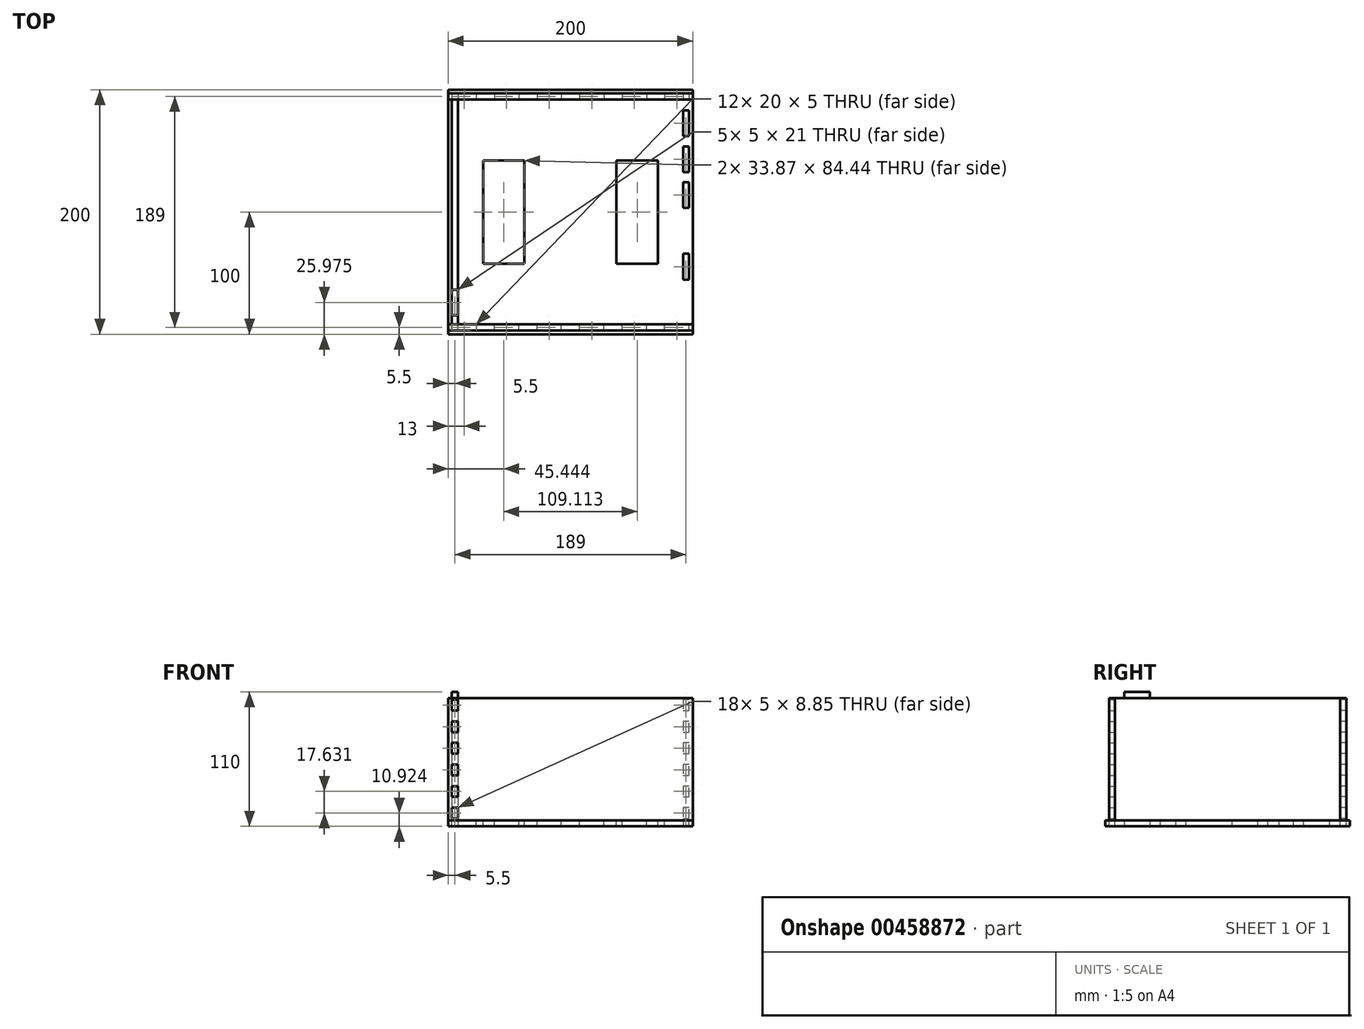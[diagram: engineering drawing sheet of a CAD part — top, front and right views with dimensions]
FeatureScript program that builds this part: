
annotation { "Feature Type Name" : "Feature", "Feature Type Description" : "" }
export const myFeature = defineFeature(function(context is Context, id is Id, definition is map)
    precondition{}
    {
        {
            assignVariable(context, id + "F0", {"name" : "width", "anyValue" : 5});
        }
        {
            var Q0;
            Q0=qCreatedBy(makeId("Top.planeOp"),FACE);
            var sketch = newSketch(context, id + "F1", { "sketchPlane" : qUnion([Q0])});
            skLineSegment(sketch, "E0.bottom", {"start": v(100, -100) * mm, "end": v(-100, -100) * mm});
            skLineSegment(sketch, "E0.top", {"start": v(100, 100) * mm, "end": v(-100, 100) * mm});
            skLineSegment(sketch, "E0.left", {"start": v(100, -100) * mm, "end": v(100, 100) * mm});
            skLineSegment(sketch, "E0.right", {"start": v(-100, -100) * mm, "end": v(-100, 100) * mm});
            skPoint(sketch, "E0.middle", {"position": v(0, 0) * mm});
            skLineSegment(sketch, "E1.0", {"start": v(97, 97) * mm, "end": v(-97, 97) * mm, "construction": true});
            skLineSegment(sketch, "E1.1", {"start": v(97, -97) * mm, "end": v(97, 97) * mm, "construction": true});
            skLineSegment(sketch, "E1.2", {"start": v(97, -97) * mm, "end": v(-97, -97) * mm, "construction": true});
            skLineSegment(sketch, "E1.3", {"start": v(-97, -97) * mm, "end": v(-97, 97) * mm, "construction": true});
            skSolve(sketch);
        }
        {
            var Q0;
            Q0 = qSketchRegion(id + "F1", true);
            extrude(context, id + "F2", {"entities" : qUnion([Q0]), "depth" : (getVariable(context, 'width')) * mm});
        }
        {
            var Q0;
            Q0=makeQuery(id+"F2.opExtrude","CAP_FACE",FACE,{"disambiguationData":[OSD([sQuery(id+"F1.wireOp",EDGE,"E0.bottom"),sQuery(id+"F1.wireOp",EDGE,"E0.top"),sQuery(id+"F1.wireOp",EDGE,"E0.left"),sQuery(id+"F1.wireOp",EDGE,"E0.right")])],"isStart":false});
            var sketch = newSketch(context, id + "F3", { "sketchPlane" : qUnion([Q0])});
            skLineSegment(sketch, "E2.0", {"start": v(97, 97) * mm, "end": v(-97, 97) * mm, "construction": true});
            skLineSegment(sketch, "E2.1", {"start": v(97, -97) * mm, "end": v(97, 97) * mm, "construction": true});
            skLineSegment(sketch, "E2.2", {"start": v(97, -97) * mm, "end": v(-97, -97) * mm, "construction": true});
            skLineSegment(sketch, "E2.3", {"start": v(-97, -97) * mm, "end": v(-97, 97) * mm, "construction": true});
            skLineSegment(sketch, "E3.bottom", {"start": v(-97, 97) * mm, "end": v(-77, 97) * mm, "construction": true});
            skLineSegment(sketch, "E3.left", {"start": v(-97, 97) * mm, "end": v(-97, 92) * mm, "construction": true});
            skLineSegment(sketch, "E4.bottom", {"start": v(-97, 97) * mm, "end": v(-77, 97) * mm});
            skLineSegment(sketch, "E4.top", {"start": v(-97, 92) * mm, "end": v(-77, 92) * mm});
            skLineSegment(sketch, "E4.left", {"start": v(-97, 97) * mm, "end": v(-97, 92) * mm});
            skLineSegment(sketch, "E4.right", {"start": v(-77, 97) * mm, "end": v(-77, 92) * mm});
            skLineSegment(sketch, "E5.1.0.0", {"start": v(-42.2, 97) * mm, "end": v(-42.2, 92) * mm});
            skLineSegment(sketch, "E5.1.0.1", {"start": v(-62.2, 92) * mm, "end": v(-42.2, 92) * mm});
            skLineSegment(sketch, "E5.1.0.2", {"start": v(-62.2, 97) * mm, "end": v(-42.2, 97) * mm});
            skLineSegment(sketch, "E5.1.0.3", {"start": v(-62.2, 97) * mm, "end": v(-62.2, 92) * mm});
            skLineSegment(sketch, "E5.2.0.0", {"start": v(-7.4, 97) * mm, "end": v(-7.4, 92) * mm});
            skLineSegment(sketch, "E5.2.0.1", {"start": v(-27.4, 92) * mm, "end": v(-7.4, 92) * mm});
            skLineSegment(sketch, "E5.2.0.2", {"start": v(-27.4, 97) * mm, "end": v(-7.4, 97) * mm});
            skLineSegment(sketch, "E5.2.0.3", {"start": v(-27.4, 97) * mm, "end": v(-27.4, 92) * mm});
            skLineSegment(sketch, "E5.3.0.0", {"start": v(27.4, 97) * mm, "end": v(27.4, 92) * mm});
            skLineSegment(sketch, "E5.3.0.1", {"start": v(7.4, 92) * mm, "end": v(27.4, 92) * mm});
            skLineSegment(sketch, "E5.3.0.2", {"start": v(7.4, 97) * mm, "end": v(27.4, 97) * mm});
            skLineSegment(sketch, "E5.3.0.3", {"start": v(7.4, 97) * mm, "end": v(7.4, 92) * mm});
            skLineSegment(sketch, "E5.4.0.0", {"start": v(62.2, 97) * mm, "end": v(62.2, 92) * mm});
            skLineSegment(sketch, "E5.4.0.1", {"start": v(42.2, 92) * mm, "end": v(62.2, 92) * mm});
            skLineSegment(sketch, "E5.4.0.2", {"start": v(42.2, 97) * mm, "end": v(62.2, 97) * mm});
            skLineSegment(sketch, "E5.4.0.3", {"start": v(42.2, 97) * mm, "end": v(42.2, 92) * mm});
            skLineSegment(sketch, "E5.5.0.0", {"start": v(97, 97) * mm, "end": v(97, 92) * mm});
            skLineSegment(sketch, "E5.5.0.1", {"start": v(77, 92) * mm, "end": v(97, 92) * mm});
            skLineSegment(sketch, "E5.5.0.2", {"start": v(77, 97) * mm, "end": v(97, 97) * mm});
            skLineSegment(sketch, "E5.5.0.3", {"start": v(77, 97) * mm, "end": v(77, 92) * mm});
            skLineSegment(sketch, "E5.direction1", {"start": v(-77, 92) * mm, "end": v(-42.2, 92) * mm, "construction": true});
            skLineSegment(sketch, "E6.MirrorCS", {"start": v(-97, -97) * mm, "end": v(-97, -92) * mm});
            skLineSegment(sketch, "E7.MirrorCS", {"start": v(-77, -97) * mm, "end": v(-77, -92) * mm});
            skLineSegment(sketch, "E8.MirrorCS", {"start": v(-97, -97) * mm, "end": v(-97, -92) * mm, "construction": true});
            skLineSegment(sketch, "E9.MirrorCS", {"start": v(97, -97) * mm, "end": v(97, -92) * mm});
            skLineSegment(sketch, "E10.MirrorCS", {"start": v(77, -97) * mm, "end": v(77, -92) * mm});
            skLineSegment(sketch, "E11.MirrorCS", {"start": v(-42.2, -97) * mm, "end": v(-42.2, -92) * mm});
            skLineSegment(sketch, "E12.MirrorCS", {"start": v(62.2, -97) * mm, "end": v(62.2, -92) * mm});
            skLineSegment(sketch, "E13.MirrorCS", {"start": v(-62.2, -97) * mm, "end": v(-62.2, -92) * mm});
            skLineSegment(sketch, "E14.MirrorCS", {"start": v(-7.4, -97) * mm, "end": v(-7.4, -92) * mm});
            skLineSegment(sketch, "E15.MirrorCS", {"start": v(-27.4, -97) * mm, "end": v(-27.4, -92) * mm});
            skLineSegment(sketch, "E16.MirrorCS", {"start": v(7.4, -97) * mm, "end": v(7.4, -92) * mm});
            skLineSegment(sketch, "E17.MirrorCS", {"start": v(27.4, -97) * mm, "end": v(27.4, -92) * mm});
            skLineSegment(sketch, "E18.MirrorCS", {"start": v(42.2, -97) * mm, "end": v(42.2, -92) * mm});
            skLineSegment(sketch, "E19.MirrorCS", {"start": v(-62.2, -92) * mm, "end": v(-42.2, -92) * mm});
            skLineSegment(sketch, "E20.MirrorCS", {"start": v(-27.4, -97) * mm, "end": v(-7.4, -97) * mm});
            skLineSegment(sketch, "E21.MirrorCS", {"start": v(7.4, -97) * mm, "end": v(27.4, -97) * mm});
            skLineSegment(sketch, "E22.MirrorCS", {"start": v(42.2, -97) * mm, "end": v(62.2, -97) * mm});
            skLineSegment(sketch, "E23.MirrorCS", {"start": v(77, -97) * mm, "end": v(97, -97) * mm});
            skLineSegment(sketch, "E24.MirrorCS", {"start": v(-62.2, -97) * mm, "end": v(-42.2, -97) * mm});
            skLineSegment(sketch, "E25.MirrorCS", {"start": v(-97, -97) * mm, "end": v(-77, -97) * mm});
            skLineSegment(sketch, "E26.MirrorCS", {"start": v(42.2, -92) * mm, "end": v(62.2, -92) * mm});
            skLineSegment(sketch, "E27.MirrorCS", {"start": v(77, -92) * mm, "end": v(97, -92) * mm});
            skLineSegment(sketch, "E28.MirrorCS", {"start": v(-77, -92) * mm, "end": v(-42.2, -92) * mm, "construction": true});
            skLineSegment(sketch, "E29.MirrorCS", {"start": v(-27.4, -92) * mm, "end": v(-7.4, -92) * mm});
            skLineSegment(sketch, "E30.MirrorCS", {"start": v(-97, -97) * mm, "end": v(-77, -97) * mm, "construction": true});
            skLineSegment(sketch, "E31.MirrorCS", {"start": v(-97, -92) * mm, "end": v(-77, -92) * mm});
            skLineSegment(sketch, "E32.MirrorCS", {"start": v(7.4, -92) * mm, "end": v(27.4, -92) * mm});
            skSolve(sketch);
        }
        {
            var Q0;
            Q0 = qSketchRegion(id + "F3", true);
            extrude(context, id + "F4", {"entities" : qUnion([Q0]), "operationType" : NewBodyOperationType.REMOVE, "oppositeDirection" : true, "depth" : 25 * mm});
        }
        {
            var Q0;
            Q0=makeQuery(id+"F2.opExtrude","CAP_FACE",FACE,{"disambiguationData":[OSD([sQuery(id+"F1.wireOp",EDGE,"E0.bottom"),sQuery(id+"F1.wireOp",EDGE,"E0.top"),sQuery(id+"F1.wireOp",EDGE,"E0.left"),sQuery(id+"F1.wireOp",EDGE,"E0.right")])],"isStart":false});
            var sketch = newSketch(context, id + "F5", { "sketchPlane" : qUnion([Q0])});
            skLineSegment(sketch, "E33.0", {"start": v(-97, 97) * mm, "end": v(-77, 97) * mm});
            skSolve(sketch);
        }
        {
            var Q0;
            Q0=makeQuery(id+"F5.imprint","IMPRINT",FACE,{"disambiguationData":[TD([[makeQuery(id+"F5.imprint","IMPRINT",EDGE,{"derivedFrom":makeQuery(id+"F4.boolean.opBoolean","COPY",EDGE,{"derivedFrom":makeQuery(id+"F4.opExtrude","CAP_EDGE",EDGE,{"disambiguationData":[OSD([sQuery(id+"F3.wireOp",EDGE,"E5.1.0.0")])],"isStart":true})})}),-1.0]])]});
            var Q1;
            Q1=makeQuery(id+"F5.imprint","IMPRINT",FACE,{"disambiguationData":[TD([[makeQuery(id+"F5.imprint","IMPRINT",EDGE,{"derivedFrom":sQuery(id+"F5.wireOp",EDGE,"E33.0")}),-1.0]])]});
            var Q2;
            Q2=makeQuery(id+"F5.imprint","IMPRINT",FACE,{"disambiguationData":[TD([[makeQuery(id+"F5.imprint","IMPRINT",EDGE,{"derivedFrom":makeQuery(id+"F4.boolean.opBoolean","COPY",EDGE,{"derivedFrom":makeQuery(id+"F4.opExtrude","CAP_EDGE",EDGE,{"disambiguationData":[OSD([sQuery(id+"F3.wireOp",EDGE,"E5.2.0.0")])],"isStart":true})})}),-1.0]])]});
            var Q3;
            Q3=makeQuery(id+"F5.imprint","IMPRINT",FACE,{"disambiguationData":[TD([[makeQuery(id+"F5.imprint","IMPRINT",EDGE,{"derivedFrom":makeQuery(id+"F4.boolean.opBoolean","COPY",EDGE,{"derivedFrom":makeQuery(id+"F4.opExtrude","CAP_EDGE",EDGE,{"disambiguationData":[OSD([sQuery(id+"F3.wireOp",EDGE,"E5.3.0.0")])],"isStart":true})})}),-1.0]])]});
            var Q4;
            Q4=makeQuery(id+"F5.imprint","IMPRINT",FACE,{"disambiguationData":[TD([[makeQuery(id+"F5.imprint","IMPRINT",EDGE,{"derivedFrom":makeQuery(id+"F4.boolean.opBoolean","COPY",EDGE,{"derivedFrom":makeQuery(id+"F4.opExtrude","CAP_EDGE",EDGE,{"disambiguationData":[OSD([sQuery(id+"F3.wireOp",EDGE,"E5.4.0.0")])],"isStart":true})})}),-1.0]])]});
            var Q5;
            Q5=makeQuery(id+"F5.imprint","IMPRINT",FACE,{"disambiguationData":[TD([[makeQuery(id+"F5.imprint","IMPRINT",EDGE,{"derivedFrom":makeQuery(id+"F4.boolean.opBoolean","COPY",EDGE,{"derivedFrom":makeQuery(id+"F4.opExtrude","CAP_EDGE",EDGE,{"disambiguationData":[OSD([sQuery(id+"F3.wireOp",EDGE,"E5.5.0.0")])],"isStart":true})})}),-1.0]])]});
            var Q6;
            Q6=makeQuery(id+"F2.opExtrude","CAP_FACE",FACE,{"disambiguationData":[OSD([sQuery(id+"F1.wireOp",EDGE,"E0.bottom"),sQuery(id+"F1.wireOp",EDGE,"E0.top"),sQuery(id+"F1.wireOp",EDGE,"E0.left"),sQuery(id+"F1.wireOp",EDGE,"E0.right")])],"isStart":true});
            extrude(context, id + "F6", {"entities" : qUnion([Q0, Q1, Q2, Q3, Q4, Q5]), "endBound" : BoundingType.UP_TO_SURFACE, "oppositeDirection" : true, "endBoundEntityFace" : qUnion([Q6]), "depth" : 25 * mm});
        }
        {
            var Q0;
            Q0=makeQuery(id+"F2.opExtrude","CAP_FACE",FACE,{"disambiguationData":[OSD([sQuery(id+"F1.wireOp",EDGE,"E0.bottom"),sQuery(id+"F1.wireOp",EDGE,"E0.top"),sQuery(id+"F1.wireOp",EDGE,"E0.left"),sQuery(id+"F1.wireOp",EDGE,"E0.right")])],"isStart":false});
            var sketch = newSketch(context, id + "F7", { "sketchPlane" : qUnion([Q0])});
            skLineSegment(sketch, "E34.bottom", {"start": v(-100, 97) * mm, "end": v(100, 97) * mm});
            skLineSegment(sketch, "E34.top", {"start": v(-100, 92) * mm, "end": v(100, 92) * mm});
            skLineSegment(sketch, "E34.left", {"start": v(-100, 97) * mm, "end": v(-100, 92) * mm});
            skLineSegment(sketch, "E34.right", {"start": v(100, 97) * mm, "end": v(100, 92) * mm});
            skSolve(sketch);
        }
        {
            var Q0;
            Q0 = qSketchRegion(id + "F7", true);
            extrude(context, id + "F8", {"entities" : qUnion([Q0]), "depth" : 100 * mm});
        }
        {
            var Q0;
            Q0=makeQuery(id+"F2.opExtrude","CAP_FACE",FACE,{"disambiguationData":[OSD([sQuery(id+"F1.wireOp",EDGE,"E0.bottom"),sQuery(id+"F1.wireOp",EDGE,"E0.top"),sQuery(id+"F1.wireOp",EDGE,"E0.left"),sQuery(id+"F1.wireOp",EDGE,"E0.right")])],"isStart":true});
            var sketch = newSketch(context, id + "F9", { "sketchPlane" : qUnion([Q0])});
            skLineSegment(sketch, "E35.0", {"start": v(97, 97) * mm, "end": v(97, -97) * mm});
            skLineSegment(sketch, "E35.1", {"start": v(97, 97) * mm, "end": v(-97, 97) * mm});
            skLineSegment(sketch, "E35.2", {"start": v(-97, 97) * mm, "end": v(-97, -97) * mm});
            skLineSegment(sketch, "E35.3", {"start": v(97, -97) * mm, "end": v(-97, -97) * mm});
            skLineSegment(sketch, "E36.bottom", {"start": v(-97, 84.52) * mm, "end": v(-92, 84.52) * mm});
            skLineSegment(sketch, "E36.top", {"start": v(-97, 63.52) * mm, "end": v(-92, 63.52) * mm});
            skLineSegment(sketch, "E36.left", {"start": v(-97, 84.52) * mm, "end": v(-97, 63.52) * mm});
            skLineSegment(sketch, "E36.right", {"start": v(-92, 84.52) * mm, "end": v(-92, 63.52) * mm});
            skLineSegment(sketch, "E37.1.0.0", {"start": v(-97, 55.22) * mm, "end": v(-97, 34.22) * mm});
            skLineSegment(sketch, "E37.1.0.1", {"start": v(-97, 55.22) * mm, "end": v(-92, 55.22) * mm});
            skLineSegment(sketch, "E37.1.0.2", {"start": v(-97, 34.22) * mm, "end": v(-92, 34.22) * mm});
            skLineSegment(sketch, "E37.1.0.3", {"start": v(-92, 55.22) * mm, "end": v(-92, 34.22) * mm});
            skLineSegment(sketch, "E37.2.0.0", {"start": v(-97, 25.91) * mm, "end": v(-97, 4.91) * mm});
            skLineSegment(sketch, "E37.2.0.1", {"start": v(-97, 25.91) * mm, "end": v(-92, 25.91) * mm});
            skLineSegment(sketch, "E37.2.0.2", {"start": v(-97, 4.91) * mm, "end": v(-92, 4.91) * mm});
            skLineSegment(sketch, "E37.2.0.3", {"start": v(-92, 25.91) * mm, "end": v(-92, 4.91) * mm});
            skLineSegment(sketch, "E37.3.0.0", {"start": v(-97, -3.4) * mm, "end": v(-97, -24.4) * mm});
            skLineSegment(sketch, "E37.3.0.1", {"start": v(-97, -3.4) * mm, "end": v(-92, -3.4) * mm});
            skLineSegment(sketch, "E37.3.0.2", {"start": v(-97, -24.4) * mm, "end": v(-92, -24.4) * mm});
            skLineSegment(sketch, "E37.3.0.3", {"start": v(-92, -3.4) * mm, "end": v(-92, -24.4) * mm});
            skLineSegment(sketch, "E37.4.0.0", {"start": v(-97, -32.7) * mm, "end": v(-97, -53.7) * mm});
            skLineSegment(sketch, "E37.4.0.1", {"start": v(-97, -32.7) * mm, "end": v(-92, -32.7) * mm});
            skLineSegment(sketch, "E37.4.0.2", {"start": v(-97, -53.7) * mm, "end": v(-92, -53.7) * mm});
            skLineSegment(sketch, "E37.4.0.3", {"start": v(-92, -32.7) * mm, "end": v(-92, -53.7) * mm});
            skLineSegment(sketch, "E37.5.0.0", {"start": v(-97, -62) * mm, "end": v(-97, -83) * mm});
            skLineSegment(sketch, "E37.5.0.1", {"start": v(-97, -62) * mm, "end": v(-92, -62) * mm});
            skLineSegment(sketch, "E37.5.0.2", {"start": v(-97, -83) * mm, "end": v(-92, -83) * mm});
            skLineSegment(sketch, "E37.5.0.3", {"start": v(-92, -62) * mm, "end": v(-92, -83) * mm});
            skLineSegment(sketch, "E37.direction1", {"start": v(-97, 63.52) * mm, "end": v(-97, 34.22) * mm, "construction": true});
            skLineSegment(sketch, "E38.MirrorCS", {"start": v(97, 84.52) * mm, "end": v(97, 63.52) * mm});
            skLineSegment(sketch, "E39.MirrorCS", {"start": v(97, 84.52) * mm, "end": v(92, 84.52) * mm});
            skLineSegment(sketch, "E40.MirrorCS", {"start": v(92, 84.52) * mm, "end": v(92, 63.52) * mm});
            skLineSegment(sketch, "E41.MirrorCS", {"start": v(97, 63.52) * mm, "end": v(92, 63.52) * mm});
            skLineSegment(sketch, "E42.MirrorCS", {"start": v(97, 55.22) * mm, "end": v(92, 55.22) * mm});
            skLineSegment(sketch, "E43.MirrorCS", {"start": v(92, 55.22) * mm, "end": v(92, 34.22) * mm});
            skLineSegment(sketch, "E44.MirrorCS", {"start": v(97, 63.52) * mm, "end": v(97, 34.22) * mm, "construction": true});
            skLineSegment(sketch, "E45.MirrorCS", {"start": v(97, 55.22) * mm, "end": v(97, 34.22) * mm});
            skLineSegment(sketch, "E46.MirrorCS", {"start": v(97, 25.91) * mm, "end": v(97, 4.91) * mm});
            skLineSegment(sketch, "E47.MirrorCS", {"start": v(97, 34.22) * mm, "end": v(92, 34.22) * mm});
            skLineSegment(sketch, "E48.MirrorCS", {"start": v(97, 25.91) * mm, "end": v(92, 25.91) * mm});
            skLineSegment(sketch, "E49.MirrorCS", {"start": v(92, 25.91) * mm, "end": v(92, 4.91) * mm});
            skLineSegment(sketch, "E50.MirrorCS", {"start": v(97, 4.91) * mm, "end": v(92, 4.91) * mm});
            skLineSegment(sketch, "E51.MirrorCS", {"start": v(97, -32.7) * mm, "end": v(92, -32.7) * mm});
            skLineSegment(sketch, "E52.MirrorCS", {"start": v(92, -32.7) * mm, "end": v(92, -53.7) * mm});
            skLineSegment(sketch, "E53.MirrorCS", {"start": v(97, -32.7) * mm, "end": v(97, -53.7) * mm});
            skLineSegment(sketch, "E54.MirrorCS", {"start": v(97, -53.7) * mm, "end": v(92, -53.7) * mm});
            skLineSegment(sketch, "E55.MirrorCS", {"start": v(97, -62) * mm, "end": v(92, -62) * mm});
            skLineSegment(sketch, "E56.MirrorCS", {"start": v(92, -62) * mm, "end": v(92, -83) * mm});
            skLineSegment(sketch, "E57.MirrorCS", {"start": v(97, -62) * mm, "end": v(97, -83) * mm});
            skLineSegment(sketch, "E58.MirrorCS", {"start": v(97, -83) * mm, "end": v(92, -83) * mm});
            skLineSegment(sketch, "E59.MirrorCS", {"start": v(92, -3.4) * mm, "end": v(92, -24.4) * mm});
            skLineSegment(sketch, "E60.MirrorCS", {"start": v(97, -3.4) * mm, "end": v(92, -3.4) * mm});
            skLineSegment(sketch, "E61.MirrorCS", {"start": v(97, -24.4) * mm, "end": v(92, -24.4) * mm});
            skLineSegment(sketch, "E62.MirrorCS", {"start": v(97, -3.4) * mm, "end": v(97, -24.4) * mm});
            skSolve(sketch);
        }
        {
            var Q0;
            Q0=makeQuery(id+"F9.imprint","IMPRINT",FACE,{"disambiguationData":[TD([[makeQuery(id+"F9.imprint","IMPRINT",EDGE,{"derivedFrom":sQuery(id+"F9.wireOp",EDGE,"E38.MirrorCS")}),-1.0]])]});
            var Q1;
            Q1=makeQuery(id+"F9.imprint","IMPRINT",FACE,{"disambiguationData":[TD([[makeQuery(id+"F9.imprint","IMPRINT",EDGE,{"derivedFrom":sQuery(id+"F9.wireOp",EDGE,"E42.MirrorCS")}),1.0]])]});
            var Q2;
            Q2=makeQuery(id+"F9.imprint","IMPRINT",FACE,{"disambiguationData":[TD([[makeQuery(id+"F9.imprint","IMPRINT",EDGE,{"derivedFrom":sQuery(id+"F9.wireOp",EDGE,"E46.MirrorCS")}),-1.0]])]});
            var Q3;
            Q3=makeQuery(id+"F9.imprint","IMPRINT",FACE,{"disambiguationData":[TD([[makeQuery(id+"F9.imprint","IMPRINT",EDGE,{"derivedFrom":sQuery(id+"F9.wireOp",EDGE,"E59.MirrorCS")}),1.0]])]});
            var Q4;
            Q4=makeQuery(id+"F9.imprint","IMPRINT",FACE,{"disambiguationData":[TD([[makeQuery(id+"F9.imprint","IMPRINT",EDGE,{"derivedFrom":sQuery(id+"F9.wireOp",EDGE,"E51.MirrorCS")}),1.0]])]});
            var Q5;
            Q5=makeQuery(id+"F9.imprint","IMPRINT",FACE,{"disambiguationData":[TD([[makeQuery(id+"F9.imprint","IMPRINT",EDGE,{"derivedFrom":sQuery(id+"F9.wireOp",EDGE,"E55.MirrorCS")}),1.0]])]});
            var Q6;
            Q6=makeQuery(id+"F9.imprint","IMPRINT",FACE,{"disambiguationData":[TD([[makeQuery(id+"F9.imprint","IMPRINT",EDGE,{"derivedFrom":sQuery(id+"F9.wireOp",EDGE,"E36.bottom")}),-1.0]])]});
            var Q7;
            Q7=makeQuery(id+"F9.imprint","IMPRINT",FACE,{"disambiguationData":[TD([[makeQuery(id+"F9.imprint","IMPRINT",EDGE,{"derivedFrom":sQuery(id+"F9.wireOp",EDGE,"E37.1.0.0")}),1.0]])]});
            var Q8;
            Q8=makeQuery(id+"F9.imprint","IMPRINT",FACE,{"disambiguationData":[TD([[makeQuery(id+"F9.imprint","IMPRINT",EDGE,{"derivedFrom":sQuery(id+"F9.wireOp",EDGE,"E37.2.0.0")}),1.0]])]});
            var Q9;
            Q9=makeQuery(id+"F9.imprint","IMPRINT",FACE,{"disambiguationData":[TD([[makeQuery(id+"F9.imprint","IMPRINT",EDGE,{"derivedFrom":sQuery(id+"F9.wireOp",EDGE,"E37.3.0.0")}),1.0]])]});
            var Q10;
            Q10=makeQuery(id+"F9.imprint","IMPRINT",FACE,{"disambiguationData":[TD([[makeQuery(id+"F9.imprint","IMPRINT",EDGE,{"derivedFrom":sQuery(id+"F9.wireOp",EDGE,"E37.4.0.0")}),1.0]])]});
            var Q11;
            Q11=makeQuery(id+"F9.imprint","IMPRINT",FACE,{"disambiguationData":[TD([[makeQuery(id+"F9.imprint","IMPRINT",EDGE,{"derivedFrom":sQuery(id+"F9.wireOp",EDGE,"E37.5.0.0")}),1.0]])]});
            extrude(context, id + "F10", {"entities" : qUnion([Q0, Q1, Q2, Q3, Q4, Q5, Q6, Q7, Q8, Q9, Q10, Q11]), "operationType" : NewBodyOperationType.REMOVE, "oppositeDirection" : true, "depth" : 25 * mm});
        }
        {
            var Q0;
            Q0=makeQuery(id+"F8.opExtrude","SWEPT_BODY",BODY,{"disambiguationData":[OSD([sQuery(id+"F7.wireOp",EDGE,"E34.bottom"),sQuery(id+"F7.wireOp",EDGE,"E34.top"),sQuery(id+"F7.wireOp",EDGE,"E34.left"),sQuery(id+"F7.wireOp",EDGE,"E34.right")])]});
            var Q1;
            Q1=makeQuery(id+"F6.opExtrude","SWEPT_BODY",BODY,{"disambiguationData":[OSD([sQuery(id+"F3.wireOp",EDGE,"E5.5.0.0"),sQuery(id+"F3.wireOp",EDGE,"E5.5.0.1"),sQuery(id+"F3.wireOp",EDGE,"E5.5.0.2"),sQuery(id+"F3.wireOp",EDGE,"E5.5.0.3")])]});
            var Q2;
            Q2=makeQuery(id+"F6.opExtrude","SWEPT_BODY",BODY,{"disambiguationData":[OSD([sQuery(id+"F3.wireOp",EDGE,"E5.4.0.0"),sQuery(id+"F3.wireOp",EDGE,"E5.4.0.1"),sQuery(id+"F3.wireOp",EDGE,"E5.4.0.2"),sQuery(id+"F3.wireOp",EDGE,"E5.4.0.3")])]});
            var Q3;
            Q3=makeQuery(id+"F6.opExtrude","SWEPT_BODY",BODY,{"disambiguationData":[OSD([sQuery(id+"F3.wireOp",EDGE,"E5.3.0.0"),sQuery(id+"F3.wireOp",EDGE,"E5.3.0.1"),sQuery(id+"F3.wireOp",EDGE,"E5.3.0.2"),sQuery(id+"F3.wireOp",EDGE,"E5.3.0.3")])]});
            var Q4;
            Q4=makeQuery(id+"F6.opExtrude","SWEPT_BODY",BODY,{"disambiguationData":[OSD([sQuery(id+"F3.wireOp",EDGE,"E5.2.0.0"),sQuery(id+"F3.wireOp",EDGE,"E5.2.0.1"),sQuery(id+"F3.wireOp",EDGE,"E5.2.0.2"),sQuery(id+"F3.wireOp",EDGE,"E5.2.0.3")])]});
            var Q5;
            Q5=makeQuery(id+"F6.opExtrude","SWEPT_BODY",BODY,{"disambiguationData":[OSD([sQuery(id+"F3.wireOp",EDGE,"E5.1.0.0"),sQuery(id+"F3.wireOp",EDGE,"E5.1.0.1"),sQuery(id+"F3.wireOp",EDGE,"E5.1.0.2"),sQuery(id+"F3.wireOp",EDGE,"E5.1.0.3")])]});
            var Q6;
            Q6=makeQuery(id+"F6.opExtrude","SWEPT_BODY",BODY,{"disambiguationData":[OSD([sQuery(id+"F3.wireOp",EDGE,"E4.top"),sQuery(id+"F3.wireOp",EDGE,"E4.left"),sQuery(id+"F3.wireOp",EDGE,"E4.right"),sQuery(id+"F5.wireOp",EDGE,"E33.0")])]});
            booleanBodies(context, id + "F11", {"operationType" : BooleanOperationType.UNION, "tools" : qUnion([Q0, Q1, Q2, Q3, Q4, Q5, Q6])});
        }
        {
            var Q0;
            Q0=makeQuery(id+"F11.opBoolean","MERGE",FACE,{"derivedFrom":[makeQuery(id+"F6.opExtrude","SWEPT_FACE",FACE,{"disambiguationData":[OSD([sQuery(id+"F3.wireOp",EDGE,"E4.top")])]}),makeQuery(id+"F6.opExtrude","SWEPT_FACE",FACE,{"disambiguationData":[OSD([sQuery(id+"F3.wireOp",EDGE,"E5.1.0.1")])]}),makeQuery(id+"F6.opExtrude","SWEPT_FACE",FACE,{"disambiguationData":[OSD([sQuery(id+"F3.wireOp",EDGE,"E5.2.0.1")])]}),makeQuery(id+"F6.opExtrude","SWEPT_FACE",FACE,{"disambiguationData":[OSD([sQuery(id+"F3.wireOp",EDGE,"E5.3.0.1")])]}),makeQuery(id+"F6.opExtrude","SWEPT_FACE",FACE,{"disambiguationData":[OSD([sQuery(id+"F3.wireOp",EDGE,"E5.4.0.1")])]}),makeQuery(id+"F6.opExtrude","SWEPT_FACE",FACE,{"disambiguationData":[OSD([sQuery(id+"F3.wireOp",EDGE,"E5.5.0.1")])]}),makeQuery(id+"F8.opExtrude","SWEPT_FACE",FACE,{"disambiguationData":[OSD([sQuery(id+"F7.wireOp",EDGE,"E34.top")])]})]});
            var sketch = newSketch(context, id + "F12", { "sketchPlane" : qUnion([Q0])});
            skLineSegment(sketch, "E63.bottom", {"start": v(-100, 105) * mm, "end": v(100, 105) * mm});
            skLineSegment(sketch, "E63.top", {"start": v(-100, 5) * mm, "end": v(100, 5) * mm});
            skLineSegment(sketch, "E63.left", {"start": v(-100, 105) * mm, "end": v(-100, 5) * mm});
            skLineSegment(sketch, "E63.right", {"start": v(100, 105) * mm, "end": v(100, 5) * mm});
            skLineSegment(sketch, "E64.bottom", {"start": v(-147, 8) * mm, "end": v(-142, 8) * mm});
            skLineSegment(sketch, "E64.top", {"start": v(-147, 18) * mm, "end": v(-142, 18) * mm});
            skLineSegment(sketch, "E64.left", {"start": v(-147, 8) * mm, "end": v(-147, 18) * mm});
            skLineSegment(sketch, "E64.right", {"start": v(-142, 8) * mm, "end": v(-142, 18) * mm});
            skLineSegment(sketch, "E65.1.0.0", {"start": v(-142, 24.8) * mm, "end": v(-142, 34.8) * mm});
            skLineSegment(sketch, "E65.1.0.1", {"start": v(-147, 34.8) * mm, "end": v(-142, 34.8) * mm});
            skLineSegment(sketch, "E65.1.0.2", {"start": v(-147, 24.8) * mm, "end": v(-147, 34.8) * mm});
            skLineSegment(sketch, "E65.1.0.3", {"start": v(-147, 24.8) * mm, "end": v(-142, 24.8) * mm});
            skLineSegment(sketch, "E65.2.0.0", {"start": v(-142, 41.6) * mm, "end": v(-142, 51.6) * mm});
            skLineSegment(sketch, "E65.2.0.1", {"start": v(-147, 51.6) * mm, "end": v(-142, 51.6) * mm});
            skLineSegment(sketch, "E65.2.0.2", {"start": v(-147, 41.6) * mm, "end": v(-147, 51.6) * mm});
            skLineSegment(sketch, "E65.2.0.3", {"start": v(-147, 41.6) * mm, "end": v(-142, 41.6) * mm});
            skLineSegment(sketch, "E65.3.0.0", {"start": v(-142, 58.4) * mm, "end": v(-142, 68.4) * mm});
            skLineSegment(sketch, "E65.3.0.1", {"start": v(-147, 68.4) * mm, "end": v(-142, 68.4) * mm});
            skLineSegment(sketch, "E65.3.0.2", {"start": v(-147, 58.4) * mm, "end": v(-147, 68.4) * mm});
            skLineSegment(sketch, "E65.3.0.3", {"start": v(-147, 58.4) * mm, "end": v(-142, 58.4) * mm});
            skLineSegment(sketch, "E65.4.0.0", {"start": v(-142, 75.2) * mm, "end": v(-142, 85.2) * mm});
            skLineSegment(sketch, "E65.4.0.1", {"start": v(-147, 85.2) * mm, "end": v(-142, 85.2) * mm});
            skLineSegment(sketch, "E65.4.0.2", {"start": v(-147, 75.2) * mm, "end": v(-147, 85.2) * mm});
            skLineSegment(sketch, "E65.4.0.3", {"start": v(-147, 75.2) * mm, "end": v(-142, 75.2) * mm});
            skLineSegment(sketch, "E65.5.0.0", {"start": v(-142, 92) * mm, "end": v(-142, 102) * mm});
            skLineSegment(sketch, "E65.5.0.1", {"start": v(-147, 102) * mm, "end": v(-142, 102) * mm});
            skLineSegment(sketch, "E65.5.0.2", {"start": v(-147, 92) * mm, "end": v(-147, 102) * mm});
            skLineSegment(sketch, "E65.5.0.3", {"start": v(-147, 92) * mm, "end": v(-142, 92) * mm});
            skLineSegment(sketch, "E65.direction1", {"start": v(-142, 8) * mm, "end": v(-142, 24.8) * mm, "construction": true});
            skLineSegment(sketch, "E66.MirrorCS", {"start": v(142, 92) * mm, "end": v(142, 102) * mm});
            skLineSegment(sketch, "E67.MirrorCS", {"start": v(147, 102) * mm, "end": v(142, 102) * mm});
            skLineSegment(sketch, "E68.MirrorCS", {"start": v(147, 92) * mm, "end": v(147, 102) * mm});
            skLineSegment(sketch, "E69.MirrorCS", {"start": v(147, 92) * mm, "end": v(142, 92) * mm});
            skLineSegment(sketch, "E70.MirrorCS", {"start": v(147, 51.6) * mm, "end": v(142, 51.6) * mm});
            skLineSegment(sketch, "E71.MirrorCS", {"start": v(147, 58.4) * mm, "end": v(142, 58.4) * mm});
            skLineSegment(sketch, "E72.MirrorCS", {"start": v(147, 75.2) * mm, "end": v(142, 75.2) * mm});
            skLineSegment(sketch, "E73.MirrorCS", {"start": v(147, 41.6) * mm, "end": v(142, 41.6) * mm});
            skLineSegment(sketch, "E74.MirrorCS", {"start": v(147, 18) * mm, "end": v(142, 18) * mm});
            skLineSegment(sketch, "E75.MirrorCS", {"start": v(147, 68.4) * mm, "end": v(142, 68.4) * mm});
            skLineSegment(sketch, "E76.MirrorCS", {"start": v(147, 85.2) * mm, "end": v(142, 85.2) * mm});
            skLineSegment(sketch, "E77.MirrorCS", {"start": v(147, 24.8) * mm, "end": v(142, 24.8) * mm});
            skLineSegment(sketch, "E78.MirrorCS", {"start": v(142, 75.2) * mm, "end": v(142, 85.2) * mm});
            skLineSegment(sketch, "E79.MirrorCS", {"start": v(147, 41.6) * mm, "end": v(147, 51.6) * mm});
            skLineSegment(sketch, "E80.MirrorCS", {"start": v(100, 5) * mm, "end": v(-100, 5) * mm});
            skLineSegment(sketch, "E81.MirrorCS", {"start": v(147, 8) * mm, "end": v(142, 8) * mm});
            skLineSegment(sketch, "E82.MirrorCS", {"start": v(147, 8) * mm, "end": v(147, 18) * mm});
            skLineSegment(sketch, "E83.MirrorCS", {"start": v(142, 8) * mm, "end": v(142, 24.8) * mm, "construction": true});
            skLineSegment(sketch, "E84.MirrorCS", {"start": v(142, 24.8) * mm, "end": v(142, 34.8) * mm});
            skLineSegment(sketch, "E85.MirrorCS", {"start": v(147, 34.8) * mm, "end": v(142, 34.8) * mm});
            skLineSegment(sketch, "E86.MirrorCS", {"start": v(147, 24.8) * mm, "end": v(147, 34.8) * mm});
            skLineSegment(sketch, "E87.MirrorCS", {"start": v(142, 41.6) * mm, "end": v(142, 51.6) * mm});
            skLineSegment(sketch, "E88.MirrorCS", {"start": v(142, 58.4) * mm, "end": v(142, 68.4) * mm});
            skLineSegment(sketch, "E89.MirrorCS", {"start": v(147, 58.4) * mm, "end": v(147, 68.4) * mm});
            skLineSegment(sketch, "E90.MirrorCS", {"start": v(147, 75.2) * mm, "end": v(147, 85.2) * mm});
            skLineSegment(sketch, "E91", {"start": v(142, 18) * mm, "end": v(142, 8) * mm});
            skSolve(sketch);
        }
        {
            var Q0;
            Q0=makeQuery(id+"F12.imprint","IMPRINT",FACE,{"disambiguationData":[TD([[makeQuery(id+"F12.imprint","IMPRINT",EDGE,{"derivedFrom":sQuery(id+"F12.wireOp",EDGE,"E65.5.0.0")}),1.0]])]});
            var Q1;
            Q1=makeQuery(id+"F12.imprint","IMPRINT",FACE,{"disambiguationData":[TD([[makeQuery(id+"F12.imprint","IMPRINT",EDGE,{"derivedFrom":sQuery(id+"F12.wireOp",EDGE,"E65.4.0.0")}),1.0]])]});
            var Q2;
            Q2=makeQuery(id+"F12.imprint","IMPRINT",FACE,{"disambiguationData":[TD([[makeQuery(id+"F12.imprint","IMPRINT",EDGE,{"derivedFrom":sQuery(id+"F12.wireOp",EDGE,"E65.3.0.0")}),1.0]])]});
            var Q3;
            Q3=makeQuery(id+"F12.imprint","IMPRINT",FACE,{"disambiguationData":[TD([[makeQuery(id+"F12.imprint","IMPRINT",EDGE,{"derivedFrom":sQuery(id+"F12.wireOp",EDGE,"E65.2.0.0")}),1.0]])]});
            var Q4;
            Q4=makeQuery(id+"F12.imprint","IMPRINT",FACE,{"disambiguationData":[TD([[makeQuery(id+"F12.imprint","IMPRINT",EDGE,{"derivedFrom":sQuery(id+"F12.wireOp",EDGE,"E65.1.0.0")}),1.0]])]});
            var Q5;
            Q5=makeQuery(id+"F12.imprint","IMPRINT",FACE,{"disambiguationData":[TD([[makeQuery(id+"F12.imprint","IMPRINT",EDGE,{"derivedFrom":sQuery(id+"F12.wireOp",EDGE,"E64.bottom")}),1.0]])]});
            var Q6;
            Q6=makeQuery(id+"F12.imprint","IMPRINT",FACE,{"disambiguationData":[TD([[makeQuery(id+"F12.imprint","IMPRINT",EDGE,{"derivedFrom":sQuery(id+"F12.wireOp",EDGE,"E66.MirrorCS")}),-1.0]])]});
            var Q7;
            Q7=makeQuery(id+"F12.imprint","IMPRINT",FACE,{"disambiguationData":[TD([[makeQuery(id+"F12.imprint","IMPRINT",EDGE,{"derivedFrom":sQuery(id+"F12.wireOp",EDGE,"E72.MirrorCS")}),-1.0]])]});
            var Q8;
            Q8=makeQuery(id+"F12.imprint","IMPRINT",FACE,{"disambiguationData":[TD([[makeQuery(id+"F12.imprint","IMPRINT",EDGE,{"derivedFrom":sQuery(id+"F12.wireOp",EDGE,"E71.MirrorCS")}),-1.0]])]});
            var Q9;
            Q9=makeQuery(id+"F12.imprint","IMPRINT",FACE,{"disambiguationData":[TD([[makeQuery(id+"F12.imprint","IMPRINT",EDGE,{"derivedFrom":sQuery(id+"F12.wireOp",EDGE,"E70.MirrorCS")}),1.0]])]});
            var Q10;
            Q10=makeQuery(id+"F12.imprint","IMPRINT",FACE,{"disambiguationData":[TD([[makeQuery(id+"F12.imprint","IMPRINT",EDGE,{"derivedFrom":sQuery(id+"F12.wireOp",EDGE,"E77.MirrorCS")}),-1.0]])]});
            var Q11;
            Q11=makeQuery(id+"F12.imprint","IMPRINT",FACE,{"disambiguationData":[TD([[makeQuery(id+"F12.imprint","IMPRINT",EDGE,{"derivedFrom":sQuery(id+"F12.wireOp",EDGE,"E82.MirrorCS")}),1.0]])]});
            extrude(context, id + "F13", {"entities" : qUnion([Q0, Q1, Q2, Q3, Q4, Q5, Q6, Q7, Q8, Q9, Q10, Q11]), "operationType" : NewBodyOperationType.REMOVE, "oppositeDirection" : true, "depth" : 25 * mm});
        }
        {
            var Q0;
            Q0=makeQuery(id+"F2.opExtrude","CAP_FACE",FACE,{"disambiguationData":[OSD([sQuery(id+"F1.wireOp",EDGE,"E0.bottom"),sQuery(id+"F1.wireOp",EDGE,"E0.top"),sQuery(id+"F1.wireOp",EDGE,"E0.left"),sQuery(id+"F1.wireOp",EDGE,"E0.right")])],"isStart":false});
            var sketch = newSketch(context, id + "F14", { "sketchPlane" : qUnion([Q0])});
            skLineSegment(sketch, "E92.bottom", {"start": v(-97, 92) * mm, "end": v(-92, 92) * mm});
            skLineSegment(sketch, "E92.top", {"start": v(-97, -92) * mm, "end": v(-92, -92) * mm});
            skLineSegment(sketch, "E92.left", {"start": v(-97, 92) * mm, "end": v(-97, -92) * mm});
            skLineSegment(sketch, "E92.right", {"start": v(-92, 92) * mm, "end": v(-92, -92) * mm});
            skSolve(sketch);
        }
        {
            var Q0;
            Q0 = qSketchRegion(id + "F14", true);
            extrude(context, id + "F15", {"entities" : qUnion([Q0]), "depth" : 100 * mm});
        }
        {
            var Q0;
            Q0=makeQuery(id+"F9.imprint","IMPRINT",FACE,{"disambiguationData":[TD([[makeQuery(id+"F9.imprint","IMPRINT",EDGE,{"derivedFrom":sQuery(id+"F9.wireOp",EDGE,"E36.bottom")}),-1.0]])]});
            var Q1;
            Q1=makeQuery(id+"F9.imprint","IMPRINT",FACE,{"disambiguationData":[TD([[makeQuery(id+"F9.imprint","IMPRINT",EDGE,{"derivedFrom":sQuery(id+"F9.wireOp",EDGE,"E37.1.0.0")}),1.0]])]});
            var Q2;
            Q2=makeQuery(id+"F9.imprint","IMPRINT",FACE,{"disambiguationData":[TD([[makeQuery(id+"F9.imprint","IMPRINT",EDGE,{"derivedFrom":sQuery(id+"F9.wireOp",EDGE,"E37.2.0.0")}),1.0]])]});
            var Q3;
            Q3=makeQuery(id+"F9.imprint","IMPRINT",FACE,{"disambiguationData":[TD([[makeQuery(id+"F9.imprint","IMPRINT",EDGE,{"derivedFrom":sQuery(id+"F9.wireOp",EDGE,"E37.3.0.0")}),1.0]])]});
            var Q4;
            Q4=makeQuery(id+"F9.imprint","IMPRINT",FACE,{"disambiguationData":[TD([[makeQuery(id+"F9.imprint","IMPRINT",EDGE,{"derivedFrom":sQuery(id+"F9.wireOp",EDGE,"E37.4.0.0")}),1.0]])]});
            var Q5;
            Q5=makeQuery(id+"F9.imprint","IMPRINT",FACE,{"disambiguationData":[TD([[makeQuery(id+"F9.imprint","IMPRINT",EDGE,{"derivedFrom":sQuery(id+"F9.wireOp",EDGE,"E37.5.0.0")}),1.0]])]});
            var Q6;
            Q6=makeQuery(id+"F2.opExtrude","CAP_FACE",FACE,{"disambiguationData":[OSD([sQuery(id+"F1.wireOp",EDGE,"E0.bottom"),sQuery(id+"F1.wireOp",EDGE,"E0.top"),sQuery(id+"F1.wireOp",EDGE,"E0.left"),sQuery(id+"F1.wireOp",EDGE,"E0.right")])],"isStart":false});
            extrude(context, id + "F16", {"entities" : qUnion([Q0, Q1, Q2, Q3, Q4, Q5]), "endBound" : BoundingType.UP_TO_SURFACE, "oppositeDirection" : true, "endBoundEntityFace" : qUnion([Q6]), "depth" : 25 * mm});
        }
        {
            var Q0;
            Q0=makeQuery(id+"F15.opExtrude","SWEPT_BODY",BODY,{"disambiguationData":[OSD([sQuery(id+"F14.wireOp",EDGE,"E92.bottom"),sQuery(id+"F14.wireOp",EDGE,"E92.top"),sQuery(id+"F14.wireOp",EDGE,"E92.left"),sQuery(id+"F14.wireOp",EDGE,"E92.right")])]});
            var Q1;
            Q1=makeQuery(id+"F16.opExtrude","SWEPT_BODY",BODY,{"disambiguationData":[OSD([sQuery(id+"F9.wireOp",EDGE,"E37.5.0.0"),sQuery(id+"F9.wireOp",EDGE,"E37.5.0.1"),sQuery(id+"F9.wireOp",EDGE,"E37.5.0.2"),sQuery(id+"F9.wireOp",EDGE,"E37.5.0.3")])]});
            var Q2;
            Q2=makeQuery(id+"F16.opExtrude","SWEPT_BODY",BODY,{"disambiguationData":[OSD([sQuery(id+"F9.wireOp",EDGE,"E37.4.0.0"),sQuery(id+"F9.wireOp",EDGE,"E37.4.0.1"),sQuery(id+"F9.wireOp",EDGE,"E37.4.0.2"),sQuery(id+"F9.wireOp",EDGE,"E37.4.0.3")])]});
            var Q3;
            Q3=makeQuery(id+"F16.opExtrude","SWEPT_BODY",BODY,{"disambiguationData":[OSD([sQuery(id+"F9.wireOp",EDGE,"E37.3.0.0"),sQuery(id+"F9.wireOp",EDGE,"E37.3.0.1"),sQuery(id+"F9.wireOp",EDGE,"E37.3.0.2"),sQuery(id+"F9.wireOp",EDGE,"E37.3.0.3")])]});
            var Q4;
            Q4=makeQuery(id+"F16.opExtrude","SWEPT_BODY",BODY,{"disambiguationData":[OSD([sQuery(id+"F9.wireOp",EDGE,"E37.2.0.0"),sQuery(id+"F9.wireOp",EDGE,"E37.2.0.1"),sQuery(id+"F9.wireOp",EDGE,"E37.2.0.2"),sQuery(id+"F9.wireOp",EDGE,"E37.2.0.3")])]});
            var Q5;
            Q5=makeQuery(id+"F16.opExtrude","SWEPT_BODY",BODY,{"disambiguationData":[OSD([sQuery(id+"F9.wireOp",EDGE,"E37.1.0.0"),sQuery(id+"F9.wireOp",EDGE,"E37.1.0.1"),sQuery(id+"F9.wireOp",EDGE,"E37.1.0.2"),sQuery(id+"F9.wireOp",EDGE,"E37.1.0.3")])]});
            var Q6;
            Q6=makeQuery(id+"F16.opExtrude","SWEPT_BODY",BODY,{"disambiguationData":[OSD([sQuery(id+"F9.wireOp",EDGE,"E36.bottom"),sQuery(id+"F9.wireOp",EDGE,"E36.top"),sQuery(id+"F9.wireOp",EDGE,"E36.left"),sQuery(id+"F9.wireOp",EDGE,"E36.right")])]});
            booleanBodies(context, id + "F17", {"operationType" : BooleanOperationType.UNION, "tools" : qUnion([Q0, Q1, Q2, Q3, Q4, Q5, Q6])});
        }
        {
            var Q0;
            Q0=makeQuery(id+"F8.opExtrude","SWEPT_BODY",BODY,{"disambiguationData":[OSD([sQuery(id+"F7.wireOp",EDGE,"E34.bottom"),sQuery(id+"F7.wireOp",EDGE,"E34.top"),sQuery(id+"F7.wireOp",EDGE,"E34.left"),sQuery(id+"F7.wireOp",EDGE,"E34.right")])]});
            transform(context, id + "F18", {"entities" : qUnion([Q0]), "transformType" : TransformType.TRANSLATION_3D, "dx" : 0 * mm, "dy" : -189 * mm, "dz" : 0 * mm, "makeCopy" : true});
        }
        {
            var Q0;
            Q0=makeQuery(id+"F11.opBoolean","MERGE",FACE,{"derivedFrom":[makeQuery(id+"F6.opExtrude","SWEPT_FACE",FACE,{"disambiguationData":[OSD([sQuery(id+"F3.wireOp",EDGE,"E4.top")])]}),makeQuery(id+"F6.opExtrude","SWEPT_FACE",FACE,{"disambiguationData":[OSD([sQuery(id+"F3.wireOp",EDGE,"E5.1.0.1")])]}),makeQuery(id+"F6.opExtrude","SWEPT_FACE",FACE,{"disambiguationData":[OSD([sQuery(id+"F3.wireOp",EDGE,"E5.2.0.1")])]}),makeQuery(id+"F6.opExtrude","SWEPT_FACE",FACE,{"disambiguationData":[OSD([sQuery(id+"F3.wireOp",EDGE,"E5.3.0.1")])]}),makeQuery(id+"F6.opExtrude","SWEPT_FACE",FACE,{"disambiguationData":[OSD([sQuery(id+"F3.wireOp",EDGE,"E5.4.0.1")])]}),makeQuery(id+"F6.opExtrude","SWEPT_FACE",FACE,{"disambiguationData":[OSD([sQuery(id+"F3.wireOp",EDGE,"E5.5.0.1")])]}),makeQuery(id+"F8.opExtrude","SWEPT_FACE",FACE,{"disambiguationData":[OSD([sQuery(id+"F7.wireOp",EDGE,"E34.top")])]})]});
            var sketch = newSketch(context, id + "F19", { "sketchPlane" : qUnion([Q0])});
            skLineSegment(sketch, "E93", {"start": v(-97, 105) * mm, "end": v(-92, 105) * mm});
            skLineSegment(sketch, "E94", {"start": v(-97, 5) * mm, "end": v(-92, 5) * mm});
            skPoint(sketch, "E95", {"position": v(-97, 103.5) * mm});
            skLineSegment(sketch, "E96.bottom", {"start": v(-97, 103.5) * mm, "end": v(-92, 103.5) * mm});
            skLineSegment(sketch, "E96.top", {"start": v(-97, 94.65) * mm, "end": v(-92, 94.65) * mm});
            skLineSegment(sketch, "E96.left", {"start": v(-97, 103.5) * mm, "end": v(-97, 94.65) * mm});
            skLineSegment(sketch, "E96.right", {"start": v(-92, 103.5) * mm, "end": v(-92, 94.65) * mm});
            skLineSegment(sketch, "E97.1.0.0", {"start": v(-97, 77.02) * mm, "end": v(-92, 77.02) * mm});
            skLineSegment(sketch, "E97.1.0.1", {"start": v(-97, 85.87) * mm, "end": v(-97, 77.02) * mm});
            skLineSegment(sketch, "E97.1.0.2", {"start": v(-97, 85.87) * mm, "end": v(-92, 85.87) * mm});
            skLineSegment(sketch, "E97.1.0.3", {"start": v(-92, 85.87) * mm, "end": v(-92, 77.02) * mm});
            skLineSegment(sketch, "E97.2.0.0", {"start": v(-97, 59.4) * mm, "end": v(-92, 59.4) * mm});
            skLineSegment(sketch, "E97.2.0.1", {"start": v(-97, 68.24) * mm, "end": v(-97, 59.4) * mm});
            skLineSegment(sketch, "E97.2.0.2", {"start": v(-97, 68.24) * mm, "end": v(-92, 68.24) * mm});
            skLineSegment(sketch, "E97.2.0.3", {"start": v(-92, 68.24) * mm, "end": v(-92, 59.4) * mm});
            skLineSegment(sketch, "E97.3.0.0", {"start": v(-97, 41.76) * mm, "end": v(-92, 41.76) * mm});
            skLineSegment(sketch, "E97.3.0.1", {"start": v(-97, 50.6) * mm, "end": v(-97, 41.76) * mm});
            skLineSegment(sketch, "E97.3.0.2", {"start": v(-97, 50.6) * mm, "end": v(-92, 50.6) * mm});
            skLineSegment(sketch, "E97.3.0.3", {"start": v(-92, 50.6) * mm, "end": v(-92, 41.76) * mm});
            skLineSegment(sketch, "E97.4.0.0", {"start": v(-97, 24.13) * mm, "end": v(-92, 24.13) * mm});
            skLineSegment(sketch, "E97.4.0.1", {"start": v(-97, 32.98) * mm, "end": v(-97, 24.13) * mm});
            skLineSegment(sketch, "E97.4.0.2", {"start": v(-97, 32.98) * mm, "end": v(-92, 32.98) * mm});
            skLineSegment(sketch, "E97.4.0.3", {"start": v(-92, 32.98) * mm, "end": v(-92, 24.13) * mm});
            skLineSegment(sketch, "E97.5.0.0", {"start": v(-97, 6.5) * mm, "end": v(-92, 6.5) * mm});
            skLineSegment(sketch, "E97.5.0.1", {"start": v(-97, 15.35) * mm, "end": v(-97, 6.5) * mm});
            skLineSegment(sketch, "E97.5.0.2", {"start": v(-97, 15.35) * mm, "end": v(-92, 15.35) * mm});
            skLineSegment(sketch, "E97.5.0.3", {"start": v(-92, 15.35) * mm, "end": v(-92, 6.5) * mm});
            skLineSegment(sketch, "E97.direction1", {"start": v(-97, 94.65) * mm, "end": v(-97, 77.02) * mm, "construction": true});
            skSolve(sketch);
        }
        {
            var Q0;
            Q0=makeQuery(id+"F19.imprint","IMPRINT",FACE,{"disambiguationData":[TD([[makeQuery(id+"F19.imprint","IMPRINT",EDGE,{"derivedFrom":sQuery(id+"F19.wireOp",EDGE,"E96.bottom")}),-1.0]])]});
            var Q1;
            Q1=makeQuery(id+"F19.imprint","IMPRINT",FACE,{"disambiguationData":[TD([[makeQuery(id+"F19.imprint","IMPRINT",EDGE,{"derivedFrom":sQuery(id+"F19.wireOp",EDGE,"E97.1.0.0")}),1.0]])]});
            var Q2;
            Q2=makeQuery(id+"F19.imprint","IMPRINT",FACE,{"disambiguationData":[TD([[makeQuery(id+"F19.imprint","IMPRINT",EDGE,{"derivedFrom":sQuery(id+"F19.wireOp",EDGE,"E97.2.0.0")}),1.0]])]});
            var Q3;
            Q3=makeQuery(id+"F19.imprint","IMPRINT",FACE,{"disambiguationData":[TD([[makeQuery(id+"F19.imprint","IMPRINT",EDGE,{"derivedFrom":sQuery(id+"F19.wireOp",EDGE,"E97.3.0.0")}),1.0]])]});
            var Q4;
            Q4=makeQuery(id+"F19.imprint","IMPRINT",FACE,{"disambiguationData":[TD([[makeQuery(id+"F19.imprint","IMPRINT",EDGE,{"derivedFrom":sQuery(id+"F19.wireOp",EDGE,"E97.4.0.0")}),1.0]])]});
            var Q5;
            Q5=makeQuery(id+"F19.imprint","IMPRINT",FACE,{"disambiguationData":[TD([[makeQuery(id+"F19.imprint","IMPRINT",EDGE,{"derivedFrom":sQuery(id+"F19.wireOp",EDGE,"E97.5.0.0")}),1.0]])]});
            extrude(context, id + "F20", {"entities" : qUnion([Q0, Q1, Q2, Q3, Q4, Q5]), "operationType" : NewBodyOperationType.REMOVE, "oppositeDirection" : true, "depth" : 25 * mm, "offsetDistance" : 25 * mm});
        }
        {
            var Q0;
            Q0 = qSketchRegion(id + "F19", true);
            var Q1;
            Q1=makeQuery(id+"F11.opBoolean","MERGE",FACE,{"derivedFrom":[makeQuery(id+"F6.opExtrude","SWEPT_FACE",FACE,{"disambiguationData":[OSD([sQuery(id+"F5.wireOp",EDGE,"E33.0")])]}),makeQuery(id+"F6.opExtrude","SWEPT_FACE",FACE,{"disambiguationData":[OSD([sQuery(id+"F3.wireOp",EDGE,"E5.1.0.2")])]}),makeQuery(id+"F6.opExtrude","SWEPT_FACE",FACE,{"disambiguationData":[OSD([sQuery(id+"F3.wireOp",EDGE,"E5.2.0.2")])]}),makeQuery(id+"F6.opExtrude","SWEPT_FACE",FACE,{"disambiguationData":[OSD([sQuery(id+"F3.wireOp",EDGE,"E5.3.0.2")])]}),makeQuery(id+"F6.opExtrude","SWEPT_FACE",FACE,{"disambiguationData":[OSD([sQuery(id+"F3.wireOp",EDGE,"E5.4.0.2")])]}),makeQuery(id+"F6.opExtrude","SWEPT_FACE",FACE,{"disambiguationData":[OSD([sQuery(id+"F3.wireOp",EDGE,"E5.5.0.2")])]}),makeQuery(id+"F8.opExtrude","SWEPT_FACE",FACE,{"disambiguationData":[OSD([sQuery(id+"F7.wireOp",EDGE,"E34.bottom")])]})]});
            extrude(context, id + "F21", {"entities" : qUnion([Q0]), "endBound" : BoundingType.UP_TO_SURFACE, "oppositeDirection" : true, "depth" : 25 * mm, "endBoundEntityFace" : qUnion([Q1]), "offsetDistance" : 25 * mm});
        }
        {
            var Q0;
            Q0=makeQuery(id+"F15.opExtrude","SWEPT_BODY",BODY,{"disambiguationData":[OSD([sQuery(id+"F14.wireOp",EDGE,"E92.bottom"),sQuery(id+"F14.wireOp",EDGE,"E92.top"),sQuery(id+"F14.wireOp",EDGE,"E92.left"),sQuery(id+"F14.wireOp",EDGE,"E92.right")])]});
            var Q1;
            Q1=makeQuery(id+"F21.opExtrude","SWEPT_BODY",BODY,{"disambiguationData":[OSD([sQuery(id+"F19.wireOp",EDGE,"E96.bottom"),sQuery(id+"F19.wireOp",EDGE,"E96.top"),sQuery(id+"F19.wireOp",EDGE,"E96.left"),sQuery(id+"F19.wireOp",EDGE,"E96.right")])]});
            var Q2;
            Q2=makeQuery(id+"F21.opExtrude","SWEPT_BODY",BODY,{"disambiguationData":[OSD([sQuery(id+"F19.wireOp",EDGE,"E97.1.0.0"),sQuery(id+"F19.wireOp",EDGE,"E97.1.0.1"),sQuery(id+"F19.wireOp",EDGE,"E97.1.0.2"),sQuery(id+"F19.wireOp",EDGE,"E97.1.0.3")])]});
            var Q3;
            Q3=makeQuery(id+"F21.opExtrude","SWEPT_BODY",BODY,{"disambiguationData":[OSD([sQuery(id+"F19.wireOp",EDGE,"E97.2.0.0"),sQuery(id+"F19.wireOp",EDGE,"E97.2.0.1"),sQuery(id+"F19.wireOp",EDGE,"E97.2.0.2"),sQuery(id+"F19.wireOp",EDGE,"E97.2.0.3")])]});
            var Q4;
            Q4=makeQuery(id+"F21.opExtrude","SWEPT_BODY",BODY,{"disambiguationData":[OSD([sQuery(id+"F19.wireOp",EDGE,"E97.3.0.0"),sQuery(id+"F19.wireOp",EDGE,"E97.3.0.1"),sQuery(id+"F19.wireOp",EDGE,"E97.3.0.2"),sQuery(id+"F19.wireOp",EDGE,"E97.3.0.3")])]});
            var Q5;
            Q5=makeQuery(id+"F21.opExtrude","SWEPT_BODY",BODY,{"disambiguationData":[OSD([sQuery(id+"F19.wireOp",EDGE,"E97.4.0.0"),sQuery(id+"F19.wireOp",EDGE,"E97.4.0.1"),sQuery(id+"F19.wireOp",EDGE,"E97.4.0.2"),sQuery(id+"F19.wireOp",EDGE,"E97.4.0.3")])]});
            var Q6;
            Q6=makeQuery(id+"F21.opExtrude","SWEPT_BODY",BODY,{"disambiguationData":[OSD([sQuery(id+"F19.wireOp",EDGE,"E97.5.0.0"),sQuery(id+"F19.wireOp",EDGE,"E97.5.0.1"),sQuery(id+"F19.wireOp",EDGE,"E97.5.0.2"),sQuery(id+"F19.wireOp",EDGE,"E97.5.0.3")])]});
            booleanBodies(context, id + "F22", {"operationType" : BooleanOperationType.UNION, "tools" : qUnion([Q0, Q1, Q2, Q3, Q4, Q5, Q6])});
        }
        {
            var Q0;
            {var subQ35=sQuery(id+"F19.wireOp",EDGE,"E93");Q0=makeQuery(id+"F19.imprint","IMPRINT",FACE,{"disambiguationData":[TD([[makeQuery(id+"F19.imprint","IMPRINT",EDGE,{"derivedFrom":subQ35}),-1.0]])]});}
            var sketch = newSketch(context, id + "F23", { "sketchPlane" : qUnion([Q0])});
            skLineSegment(sketch, "E98.MirrorCS", {"start": v(92, 94.65) * mm, "end": v(92, 103.5) * mm});
            skLineSegment(sketch, "E99.MirrorCS", {"start": v(92, 103.5) * mm, "end": v(97, 103.5) * mm});
            skLineSegment(sketch, "E100.MirrorCS", {"start": v(97, 103.5) * mm, "end": v(97, 94.65) * mm});
            skLineSegment(sketch, "E101.MirrorCS", {"start": v(97, 94.65) * mm, "end": v(92, 94.65) * mm});
            skLineSegment(sketch, "E102.MirrorCS", {"start": v(97, 77.02) * mm, "end": v(92, 77.02) * mm});
            skLineSegment(sketch, "E103.MirrorCS", {"start": v(97, 85.87) * mm, "end": v(97, 77.02) * mm});
            skLineSegment(sketch, "E104.MirrorCS", {"start": v(92, 77.02) * mm, "end": v(92, 85.87) * mm});
            skLineSegment(sketch, "E105.MirrorCS", {"start": v(92, 85.87) * mm, "end": v(97, 85.87) * mm});
            skLineSegment(sketch, "E106.MirrorCS", {"start": v(92, 32.98) * mm, "end": v(97, 32.98) * mm});
            skLineSegment(sketch, "E107.MirrorCS", {"start": v(92, 68.24) * mm, "end": v(97, 68.24) * mm});
            skLineSegment(sketch, "E108.MirrorCS", {"start": v(97, 6.5) * mm, "end": v(92, 6.5) * mm});
            skLineSegment(sketch, "E109.MirrorCS", {"start": v(92, 15.35) * mm, "end": v(97, 15.35) * mm});
            skLineSegment(sketch, "E110.MirrorCS", {"start": v(97, 59.4) * mm, "end": v(92, 59.4) * mm});
            skLineSegment(sketch, "E111.MirrorCS", {"start": v(97, 41.76) * mm, "end": v(92, 41.76) * mm});
            skLineSegment(sketch, "E112.MirrorCS", {"start": v(97, 24.13) * mm, "end": v(92, 24.13) * mm});
            skLineSegment(sketch, "E113.MirrorCS", {"start": v(92, 50.6) * mm, "end": v(97, 50.6) * mm});
            skLineSegment(sketch, "E114.MirrorCS", {"start": v(92, 59.4) * mm, "end": v(92, 68.24) * mm});
            skLineSegment(sketch, "E115.MirrorCS", {"start": v(92, 41.76) * mm, "end": v(92, 50.6) * mm});
            skLineSegment(sketch, "E116.MirrorCS", {"start": v(92, 24.13) * mm, "end": v(92, 32.98) * mm});
            skLineSegment(sketch, "E117.MirrorCS", {"start": v(97, 50.6) * mm, "end": v(97, 41.76) * mm});
            skLineSegment(sketch, "E118.MirrorCS", {"start": v(92, 6.5) * mm, "end": v(92, 15.35) * mm});
            skLineSegment(sketch, "E119.MirrorCS", {"start": v(97, 15.35) * mm, "end": v(97, 6.5) * mm});
            skLineSegment(sketch, "E120.MirrorCS", {"start": v(97, 68.24) * mm, "end": v(97, 59.4) * mm});
            skLineSegment(sketch, "E121.MirrorCS", {"start": v(97, 32.98) * mm, "end": v(97, 24.13) * mm});
            skSolve(sketch);
        }
        {
            var Q0;
            Q0 = qSketchRegion(id + "F23", true);
            extrude(context, id + "F24", {"entities" : qUnion([Q0]), "operationType" : NewBodyOperationType.REMOVE, "oppositeDirection" : true, "depth" : 25 * mm, "offsetDistance" : 25 * mm});
        }
        {
            var Q0;
            Q0=makeQuery(id+"F18.opPattern","COPY",FACE,{"derivedFrom":makeQuery(id+"F11.opBoolean","MERGE",FACE,{"derivedFrom":[makeQuery(id+"F6.opExtrude","SWEPT_FACE",FACE,{"disambiguationData":[OSD([sQuery(id+"F5.wireOp",EDGE,"E33.0")])]}),makeQuery(id+"F6.opExtrude","SWEPT_FACE",FACE,{"disambiguationData":[OSD([sQuery(id+"F3.wireOp",EDGE,"E5.1.0.2")])]}),makeQuery(id+"F6.opExtrude","SWEPT_FACE",FACE,{"disambiguationData":[OSD([sQuery(id+"F3.wireOp",EDGE,"E5.2.0.2")])]}),makeQuery(id+"F6.opExtrude","SWEPT_FACE",FACE,{"disambiguationData":[OSD([sQuery(id+"F3.wireOp",EDGE,"E5.3.0.2")])]}),makeQuery(id+"F6.opExtrude","SWEPT_FACE",FACE,{"disambiguationData":[OSD([sQuery(id+"F3.wireOp",EDGE,"E5.4.0.2")])]}),makeQuery(id+"F6.opExtrude","SWEPT_FACE",FACE,{"disambiguationData":[OSD([sQuery(id+"F3.wireOp",EDGE,"E5.5.0.2")])]}),makeQuery(id+"F8.opExtrude","SWEPT_FACE",FACE,{"disambiguationData":[OSD([sQuery(id+"F7.wireOp",EDGE,"E34.bottom")])]})]}),"instanceName":"1"});
            var sketch = newSketch(context, id + "F25", { "sketchPlane" : qUnion([Q0])});
            skLineSegment(sketch, "E122.0", {"start": v(97, 105) * mm, "end": v(92, 105) * mm});
            skLineSegment(sketch, "E123", {"start": v(97, 5) * mm, "end": v(92, 5) * mm});
            skPoint(sketch, "E124", {"position": v(91.95, 103.5) * mm});
            skLineSegment(sketch, "E125.bottom", {"start": v(91.95, 103.5) * mm, "end": v(96.95, 103.5) * mm});
            skLineSegment(sketch, "E125.top", {"start": v(91.95, 94.66) * mm, "end": v(96.95, 94.66) * mm});
            skLineSegment(sketch, "E125.left", {"start": v(91.95, 103.5) * mm, "end": v(91.95, 94.66) * mm});
            skLineSegment(sketch, "E125.right", {"start": v(96.95, 103.5) * mm, "end": v(96.95, 94.66) * mm});
            skLineSegment(sketch, "E126.1.0.0", {"start": v(91.95, 85.87) * mm, "end": v(96.95, 85.87) * mm});
            skLineSegment(sketch, "E126.1.0.1", {"start": v(96.95, 85.87) * mm, "end": v(96.95, 77.02) * mm});
            skLineSegment(sketch, "E126.1.0.2", {"start": v(91.95, 85.87) * mm, "end": v(91.95, 77.02) * mm});
            skLineSegment(sketch, "E126.1.0.3", {"start": v(91.95, 77.02) * mm, "end": v(96.95, 77.02) * mm});
            skLineSegment(sketch, "E126.2.0.0", {"start": v(91.95, 68.24) * mm, "end": v(96.95, 68.24) * mm});
            skLineSegment(sketch, "E126.2.0.1", {"start": v(96.95, 68.24) * mm, "end": v(96.95, 59.4) * mm});
            skLineSegment(sketch, "E126.2.0.2", {"start": v(91.95, 68.24) * mm, "end": v(91.95, 59.4) * mm});
            skLineSegment(sketch, "E126.2.0.3", {"start": v(91.95, 59.4) * mm, "end": v(96.95, 59.4) * mm});
            skLineSegment(sketch, "E126.3.0.0", {"start": v(91.95, 50.6) * mm, "end": v(96.95, 50.6) * mm});
            skLineSegment(sketch, "E126.3.0.1", {"start": v(96.95, 50.6) * mm, "end": v(96.95, 41.76) * mm});
            skLineSegment(sketch, "E126.3.0.2", {"start": v(91.95, 50.6) * mm, "end": v(91.95, 41.76) * mm});
            skLineSegment(sketch, "E126.3.0.3", {"start": v(91.95, 41.76) * mm, "end": v(96.95, 41.76) * mm});
            skLineSegment(sketch, "E126.4.0.0", {"start": v(91.95, 32.98) * mm, "end": v(96.95, 32.98) * mm});
            skLineSegment(sketch, "E126.4.0.1", {"start": v(96.95, 32.98) * mm, "end": v(96.95, 24.13) * mm});
            skLineSegment(sketch, "E126.4.0.2", {"start": v(91.95, 32.98) * mm, "end": v(91.95, 24.13) * mm});
            skLineSegment(sketch, "E126.4.0.3", {"start": v(91.95, 24.13) * mm, "end": v(96.95, 24.13) * mm});
            skLineSegment(sketch, "E126.5.0.0", {"start": v(91.95, 15.35) * mm, "end": v(96.95, 15.35) * mm});
            skLineSegment(sketch, "E126.5.0.1", {"start": v(96.95, 15.35) * mm, "end": v(96.95, 6.5) * mm});
            skLineSegment(sketch, "E126.5.0.2", {"start": v(91.95, 15.35) * mm, "end": v(91.95, 6.5) * mm});
            skLineSegment(sketch, "E126.5.0.3", {"start": v(91.95, 6.5) * mm, "end": v(96.95, 6.5) * mm});
            skLineSegment(sketch, "E126.direction1", {"start": v(91.95, 103.5) * mm, "end": v(91.95, 85.87) * mm, "construction": true});
            skSolve(sketch);
        }
        {
            var Q0;
            Q0=makeQuery(id+"F25.imprint","IMPRINT",FACE,{"disambiguationData":[TD([[makeQuery(id+"F25.imprint","IMPRINT",EDGE,{"derivedFrom":sQuery(id+"F25.wireOp",EDGE,"E125.bottom")}),-1.0]])]});
            var Q1;
            Q1=makeQuery(id+"F25.imprint","IMPRINT",FACE,{"disambiguationData":[TD([[makeQuery(id+"F25.imprint","IMPRINT",EDGE,{"derivedFrom":sQuery(id+"F25.wireOp",EDGE,"E126.1.0.0")}),-1.0]])]});
            var Q2;
            Q2=makeQuery(id+"F25.imprint","IMPRINT",FACE,{"disambiguationData":[TD([[makeQuery(id+"F25.imprint","IMPRINT",EDGE,{"derivedFrom":sQuery(id+"F25.wireOp",EDGE,"E126.2.0.0")}),-1.0]])]});
            var Q3;
            Q3=makeQuery(id+"F25.imprint","IMPRINT",FACE,{"disambiguationData":[TD([[makeQuery(id+"F25.imprint","IMPRINT",EDGE,{"derivedFrom":sQuery(id+"F25.wireOp",EDGE,"E126.3.0.0")}),-1.0]])]});
            var Q4;
            Q4=makeQuery(id+"F25.imprint","IMPRINT",FACE,{"disambiguationData":[TD([[makeQuery(id+"F25.imprint","IMPRINT",EDGE,{"derivedFrom":sQuery(id+"F25.wireOp",EDGE,"E126.4.0.0")}),-1.0]])]});
            var Q5;
            Q5=makeQuery(id+"F25.imprint","IMPRINT",FACE,{"disambiguationData":[TD([[makeQuery(id+"F25.imprint","IMPRINT",EDGE,{"derivedFrom":sQuery(id+"F25.wireOp",EDGE,"E126.5.0.0")}),-1.0]])]});
            extrude(context, id + "F26", {"entities" : qUnion([Q0, Q1, Q2, Q3, Q4, Q5]), "operationType" : NewBodyOperationType.REMOVE, "oppositeDirection" : true, "depth" : 25 * mm, "offsetDistance" : 25 * mm});
        }
        {
            var Q0;
            Q0=makeQuery(id+"F25.imprint","IMPRINT",FACE,{"disambiguationData":[TD([[makeQuery(id+"F25.imprint","IMPRINT",EDGE,{"derivedFrom":sQuery(id+"F25.wireOp",EDGE,"E125.bottom")}),-1.0]])]});
            var Q1;
            Q1=makeQuery(id+"F25.imprint","IMPRINT",FACE,{"disambiguationData":[TD([[makeQuery(id+"F25.imprint","IMPRINT",EDGE,{"derivedFrom":sQuery(id+"F25.wireOp",EDGE,"E126.1.0.0")}),-1.0]])]});
            var Q2;
            Q2=makeQuery(id+"F25.imprint","IMPRINT",FACE,{"disambiguationData":[TD([[makeQuery(id+"F25.imprint","IMPRINT",EDGE,{"derivedFrom":sQuery(id+"F25.wireOp",EDGE,"E126.2.0.0")}),-1.0]])]});
            var Q3;
            Q3=makeQuery(id+"F25.imprint","IMPRINT",FACE,{"disambiguationData":[TD([[makeQuery(id+"F25.imprint","IMPRINT",EDGE,{"derivedFrom":sQuery(id+"F25.wireOp",EDGE,"E126.3.0.0")}),-1.0]])]});
            var Q4;
            Q4=makeQuery(id+"F25.imprint","IMPRINT",FACE,{"disambiguationData":[TD([[makeQuery(id+"F25.imprint","IMPRINT",EDGE,{"derivedFrom":sQuery(id+"F25.wireOp",EDGE,"E126.4.0.0")}),-1.0]])]});
            var Q5;
            Q5=makeQuery(id+"F25.imprint","IMPRINT",FACE,{"disambiguationData":[TD([[makeQuery(id+"F25.imprint","IMPRINT",EDGE,{"derivedFrom":sQuery(id+"F25.wireOp",EDGE,"E126.5.0.0")}),-1.0]])]});
            var Q6;
            Q6=makeQuery(id+"F18.opPattern","COPY",FACE,{"derivedFrom":makeQuery(id+"F11.opBoolean","MERGE",FACE,{"derivedFrom":[makeQuery(id+"F6.opExtrude","SWEPT_FACE",FACE,{"disambiguationData":[OSD([sQuery(id+"F3.wireOp",EDGE,"E4.top")])]}),makeQuery(id+"F6.opExtrude","SWEPT_FACE",FACE,{"disambiguationData":[OSD([sQuery(id+"F3.wireOp",EDGE,"E5.1.0.1")])]}),makeQuery(id+"F6.opExtrude","SWEPT_FACE",FACE,{"disambiguationData":[OSD([sQuery(id+"F3.wireOp",EDGE,"E5.2.0.1")])]}),makeQuery(id+"F6.opExtrude","SWEPT_FACE",FACE,{"disambiguationData":[OSD([sQuery(id+"F3.wireOp",EDGE,"E5.3.0.1")])]}),makeQuery(id+"F6.opExtrude","SWEPT_FACE",FACE,{"disambiguationData":[OSD([sQuery(id+"F3.wireOp",EDGE,"E5.4.0.1")])]}),makeQuery(id+"F6.opExtrude","SWEPT_FACE",FACE,{"disambiguationData":[OSD([sQuery(id+"F3.wireOp",EDGE,"E5.5.0.1")])]}),makeQuery(id+"F8.opExtrude","SWEPT_FACE",FACE,{"disambiguationData":[OSD([sQuery(id+"F7.wireOp",EDGE,"E34.top")])]})]}),"instanceName":"1"});
            extrude(context, id + "F27", {"entities" : qUnion([Q0, Q1, Q2, Q3, Q4, Q5]), "endBound" : BoundingType.UP_TO_SURFACE, "oppositeDirection" : true, "depth" : 25 * mm, "endBoundEntityFace" : qUnion([Q6]), "offsetDistance" : 25 * mm});
        }
        {
            var Q0;
            Q0=makeQuery(id+"F2.opExtrude","CAP_FACE",FACE,{"disambiguationData":[OSD([sQuery(id+"F1.wireOp",EDGE,"E0.bottom"),sQuery(id+"F1.wireOp",EDGE,"E0.top"),sQuery(id+"F1.wireOp",EDGE,"E0.left"),sQuery(id+"F1.wireOp",EDGE,"E0.right")])],"isStart":false});
            var sketch = newSketch(context, id + "F28", { "sketchPlane" : qUnion([Q0])});
            skLineSegment(sketch, "E127.bottom", {"start": v(-37.62, -42.22) * mm, "end": v(-71.5, -42.22) * mm});
            skLineSegment(sketch, "E127.top", {"start": v(-37.62, 42.22) * mm, "end": v(-71.5, 42.22) * mm});
            skLineSegment(sketch, "E127.left", {"start": v(-37.62, -42.22) * mm, "end": v(-37.62, 42.22) * mm});
            skLineSegment(sketch, "E127.right", {"start": v(-71.5, -42.22) * mm, "end": v(-71.5, 42.22) * mm});
            skPoint(sketch, "E127.middle", {"position": v(-54.56, 0) * mm});
            skLineSegment(sketch, "E128.MirrorCS", {"start": v(37.62, -42.22) * mm, "end": v(37.62, 42.22) * mm});
            skLineSegment(sketch, "E129.MirrorCS", {"start": v(37.62, 42.22) * mm, "end": v(71.5, 42.22) * mm});
            skLineSegment(sketch, "E130.MirrorCS", {"start": v(71.5, -42.22) * mm, "end": v(71.5, 42.22) * mm});
            skLineSegment(sketch, "E131.MirrorCS", {"start": v(37.62, -42.22) * mm, "end": v(71.5, -42.22) * mm});
            skSolve(sketch);
        }
        {
            var Q0;
            Q0=makeQuery(id+"F28.imprint","IMPRINT",FACE,{"disambiguationData":[TD([[makeQuery(id+"F28.imprint","IMPRINT",EDGE,{"derivedFrom":sQuery(id+"F28.wireOp",EDGE,"E127.bottom")}),-1.0]])]});
            var Q1;
            Q1=makeQuery(id+"F28.imprint","IMPRINT",FACE,{"disambiguationData":[TD([[makeQuery(id+"F28.imprint","IMPRINT",EDGE,{"derivedFrom":sQuery(id+"F28.wireOp",EDGE,"E129.MirrorCS")}),-1.0]])]});
            extrude(context, id + "F29", {"entities" : qUnion([Q0, Q1]), "operationType" : NewBodyOperationType.REMOVE, "oppositeDirection" : true, "depth" : 25 * mm, "offsetDistance" : 25 * mm});
        }
        {
            var Q0;
            Q0=makeQuery(id+"F15.opExtrude","CAP_FACE",FACE,{"disambiguationData":[OSD([sQuery(id+"F14.wireOp",EDGE,"E92.bottom"),sQuery(id+"F14.wireOp",EDGE,"E92.top"),sQuery(id+"F14.wireOp",EDGE,"E92.left"),sQuery(id+"F14.wireOp",EDGE,"E92.right")])],"isStart":false});
            cPlane(context, id + "F30", {"entities" : qUnion([Q0]), "cplaneType" : CPlaneType.OFFSET, "offset" : 50 * mm, "oppositeDirection" : true, "width" : 150 * mm, "height" : 150 * mm});
        }
        {
            var Q0;
            Q0=makeQuery(id+"F15.opExtrude","SWEPT_BODY",BODY,{"disambiguationData":[OSD([sQuery(id+"F14.wireOp",EDGE,"E92.bottom"),sQuery(id+"F14.wireOp",EDGE,"E92.top"),sQuery(id+"F14.wireOp",EDGE,"E92.left"),sQuery(id+"F14.wireOp",EDGE,"E92.right")])]});
            var Q1;
            Q1=qCreatedBy(id+"F30.planeOp",FACE);
            mirror(context, id + "F31", {"entities" : qUnion([Q0]), "mirrorPlane" : qUnion([Q1])});
        }
    });
